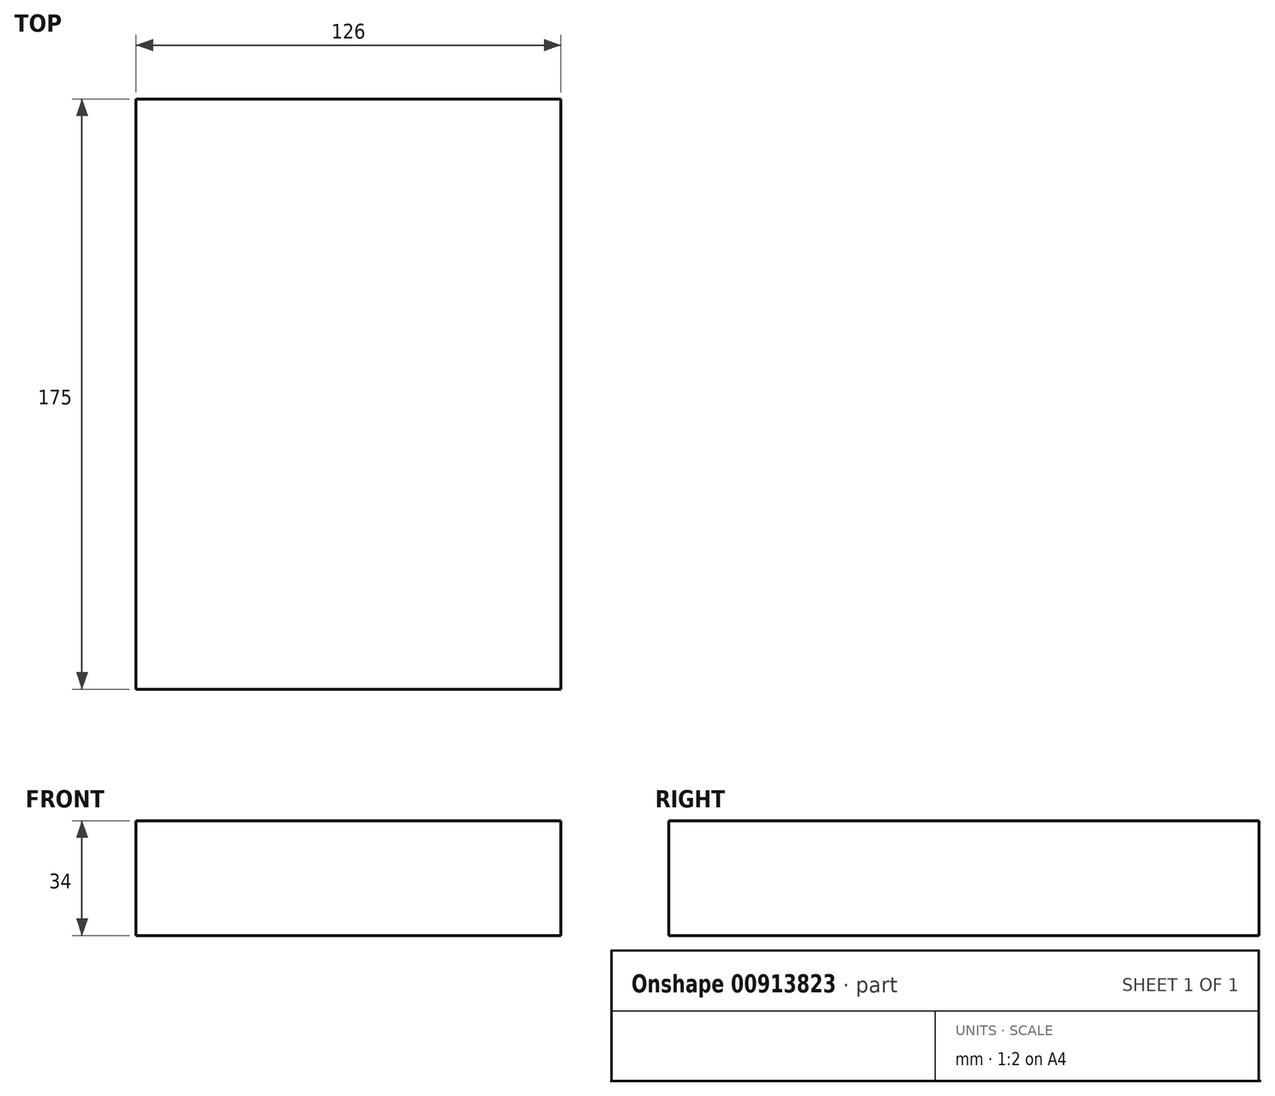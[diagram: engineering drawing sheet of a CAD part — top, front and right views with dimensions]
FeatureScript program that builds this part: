
annotation { "Feature Type Name" : "Feature", "Feature Type Description" : "" }
export const myFeature = defineFeature(function(context is Context, id is Id, definition is map)
    precondition{}
    {
        {
            var Q0;
            Q0=qCreatedBy(makeId("Top.planeOp"),FACE);
            var sketch = newSketch(context, id + "F0", { "sketchPlane" : qUnion([Q0])});
            skLineSegment(sketch, "E0.bottom", {"start": v(63, -87.5) * mm, "end": v(-63, -87.5) * mm});
            skLineSegment(sketch, "E0.top", {"start": v(63, 87.5) * mm, "end": v(-63, 87.5) * mm});
            skLineSegment(sketch, "E0.left", {"start": v(63, -87.5) * mm, "end": v(63, 87.5) * mm});
            skLineSegment(sketch, "E0.right", {"start": v(-63, -87.5) * mm, "end": v(-63, 87.5) * mm});
            skPoint(sketch, "E0.middle", {"position": v(0, 0) * mm});
            skSolve(sketch);
        }
        {
            var Q0;
            Q0=makeQuery(id+"F0.imprint","IMPRINT",FACE,{"disambiguationData":[TD([[makeQuery(id+"F0.imprint","IMPRINT",EDGE,{"derivedFrom":sQuery(id+"F0.wireOp",EDGE,"E0.bottom")}),-1.0]])]});
            extrude(context, id + "F1", {"entities" : qUnion([Q0]), "depth" : 34 * mm, "offsetDistance" : 25 * mm});
        }
    });
